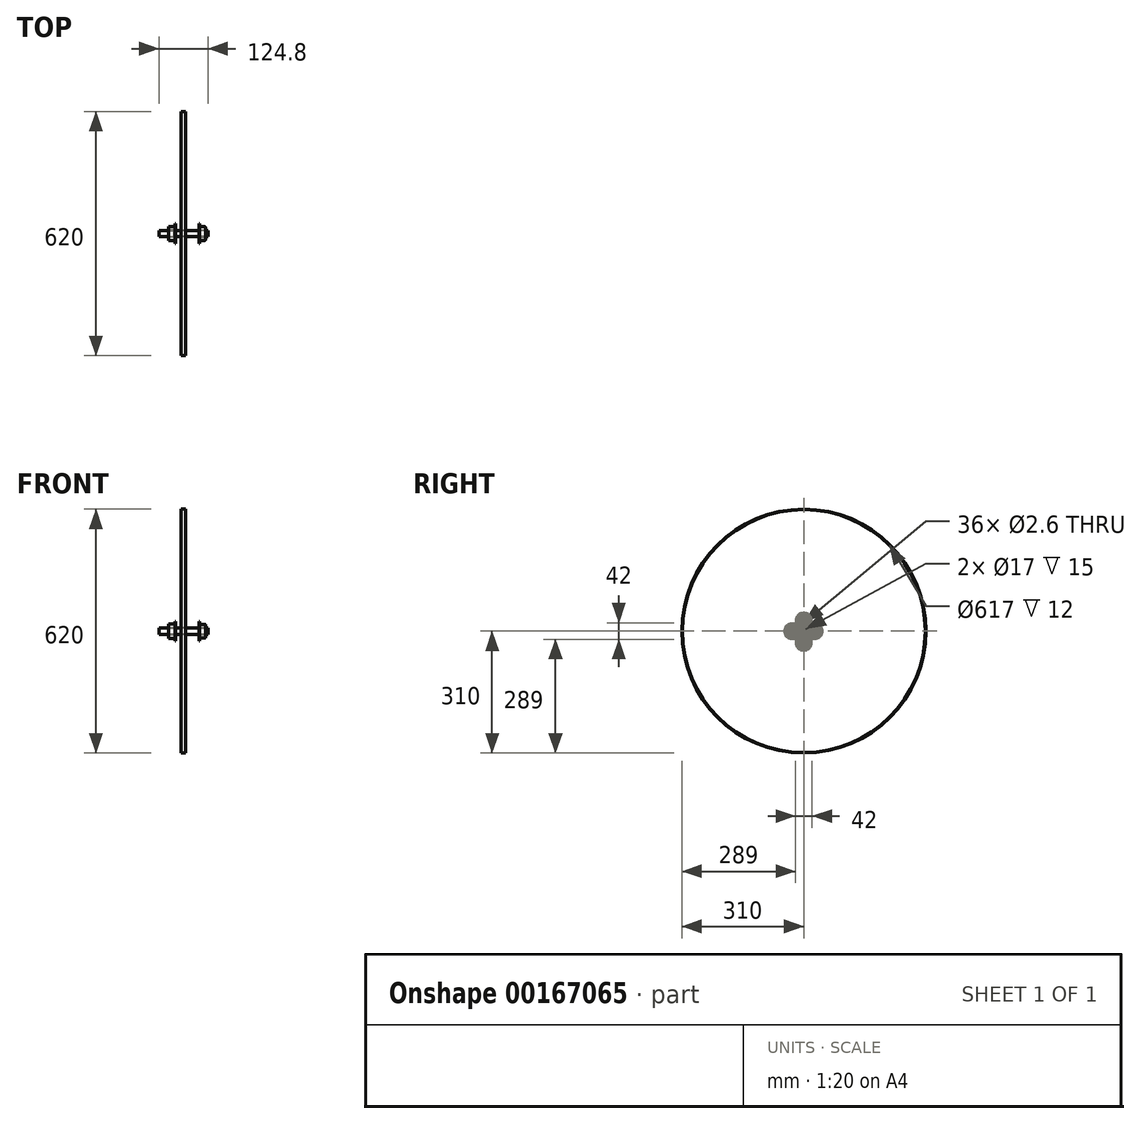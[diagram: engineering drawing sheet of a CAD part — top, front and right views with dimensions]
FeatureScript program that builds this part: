
annotation { "Feature Type Name" : "Feature", "Feature Type Description" : "" }
export const myFeature = defineFeature(function(context is Context, id is Id, definition is map)
    precondition{}
    {
        {
            var Q0;
            Q0=qCreatedBy(makeId("Top.planeOp"),FACE);
            var sketch = newSketch(context, id + "F0", { "sketchPlane" : qUnion([Q0])});
            skLineSegment(sketch, "E0", {"start": v(0, 0) * mm, "end": v(0, 18.2) * mm});
            skLineSegment(sketch, "E1", {"start": v(0, 18.2) * mm, "end": v(16.7, 18.2) * mm});
            skLineSegment(sketch, "E2", {"start": v(16.7, 18.2) * mm, "end": v(16.7, 25) * mm});
            skLineSegment(sketch, "E3", {"start": v(16.7, 25) * mm, "end": v(19, 25) * mm});
            skLineSegment(sketch, "E4", {"start": v(19, 25) * mm, "end": v(19, 8) * mm});
            skLineSegment(sketch, "E5", {"start": v(19, 8) * mm, "end": v(77.5, 8) * mm});
            skLineSegment(sketch, "E6", {"start": v(77.5, 8) * mm, "end": v(77.5, 25) * mm});
            skLineSegment(sketch, "E7", {"start": v(77.5, 25) * mm, "end": v(79.8, 25) * mm});
            skLineSegment(sketch, "E8", {"start": v(79.8, 25) * mm, "end": v(79.8, 17.6) * mm});
            skLineSegment(sketch, "E9", {"start": v(79.8, 17.6) * mm, "end": v(94.5, 17.6) * mm});
            skLineSegment(sketch, "E10", {"start": v(94.5, 17.6) * mm, "end": v(94.5, 0) * mm});
            skLineSegment(sketch, "E11", {"start": v(0, 0) * mm, "end": v(94.5, 0) * mm, "construction": true});
            skLineSegment(sketch, "E12", {"start": v(0, 0) * mm, "end": v(94.5, 0) * mm});
            skSolve(sketch);
        }
        {
            var Q0;
            Q0=makeQuery(id+"F0.imprint","IMPRINT",FACE,{"disambiguationData":[TD([[makeQuery(id+"F0.imprint","IMPRINT",EDGE,{"derivedFrom":sQuery(id+"F0.wireOp",EDGE,"E0")}),-1.0]])]});
            var Q1;
            Q1=sQuery(id+"F0.wireOp",EDGE,"E12");
            revolve(context, id + "F1", {"entities" : qUnion([Q0]), "axis" : qUnion([Q1]), "revolveType" : RevolveType.FULL});
        }
        {
            var Q0;
            Q0=makeQuery(id+"F1.opRevolve","SWEPT_FACE",FACE,{"disambiguationData":[OSD([sQuery(id+"F0.wireOp",EDGE,"E8")])]});
            var sketch = newSketch(context, id + "F2", { "sketchPlane" : qUnion([Q0])});
            skCircle(sketch, "E13", {"center": v(0, 21) * mm, "radius": 1.3 * mm});
            skCircle(sketch, "E14.1.0", {"center": v(-7.18, 19.73) * mm, "radius": 1.3 * mm});
            skCircle(sketch, "E14.2.0", {"center": v(-13.5, 16.09) * mm, "radius": 1.3 * mm});
            skCircle(sketch, "E14.3.0", {"center": v(-18.19, 10.5) * mm, "radius": 1.3 * mm});
            skCircle(sketch, "E14.4.0", {"center": v(-20.68, 3.65) * mm, "radius": 1.3 * mm});
            skCircle(sketch, "E14.5.0", {"center": v(-20.68, -3.65) * mm, "radius": 1.3 * mm});
            skCircle(sketch, "E14.6.0", {"center": v(-18.19, -10.5) * mm, "radius": 1.3 * mm});
            skCircle(sketch, "E14.7.0", {"center": v(-13.5, -16.09) * mm, "radius": 1.3 * mm});
            skCircle(sketch, "E14.8.0", {"center": v(-7.18, -19.73) * mm, "radius": 1.3 * mm});
            skCircle(sketch, "E14.9.0", {"center": v(0, -21) * mm, "radius": 1.3 * mm});
            skCircle(sketch, "E14.10.0", {"center": v(7.18, -19.73) * mm, "radius": 1.3 * mm});
            skCircle(sketch, "E14.11.0", {"center": v(13.5, -16.09) * mm, "radius": 1.3 * mm});
            skCircle(sketch, "E14.12.0", {"center": v(18.19, -10.5) * mm, "radius": 1.3 * mm});
            skCircle(sketch, "E14.13.0", {"center": v(20.68, -3.65) * mm, "radius": 1.3 * mm});
            skCircle(sketch, "E14.14.0", {"center": v(20.68, 3.65) * mm, "radius": 1.3 * mm});
            skCircle(sketch, "E14.15.0", {"center": v(18.19, 10.5) * mm, "radius": 1.3 * mm});
            skCircle(sketch, "E14.16.0", {"center": v(13.5, 16.09) * mm, "radius": 1.3 * mm});
            skCircle(sketch, "E14.17.0", {"center": v(7.18, 19.73) * mm, "radius": 1.3 * mm});
            skPoint(sketch, "E14.center", {"position": v(0, 0) * mm});
            skSolve(sketch);
        }
        {
            var Q0;
            Q0 = qSketchRegion(id + "F2", true);
            extrude(context, id + "F3", {"entities" : qUnion([Q0]), "operationType" : NewBodyOperationType.REMOVE, "endBound" : BoundingType.UP_TO_NEXT, "oppositeDirection" : true, "depth" : 25 * mm});
        }
        {
            var Q0;
            Q0=makeQuery(id+"F1.opRevolve","SWEPT_FACE",FACE,{"disambiguationData":[OSD([sQuery(id+"F0.wireOp",EDGE,"E2")])]});
            var sketch = newSketch(context, id + "F4", { "sketchPlane" : qUnion([Q0])});
            skCircle(sketch, "E15", {"center": v(0, 0) * mm, "radius": 21 * mm, "construction": true});
            skCircle(sketch, "E16", {"center": v(3.65, 20.68) * mm, "radius": 1.3 * mm});
            skLineSegment(sketch, "E17", {"start": v(3.65, 20.68) * mm, "end": v(0, 0) * mm, "construction": true});
            skCircle(sketch, "E18.1.0", {"center": v(-3.65, 20.68) * mm, "radius": 1.3 * mm});
            skCircle(sketch, "E18.2.0", {"center": v(-10.5, 18.19) * mm, "radius": 1.3 * mm});
            skCircle(sketch, "E18.3.0", {"center": v(-16.09, 13.5) * mm, "radius": 1.3 * mm});
            skCircle(sketch, "E18.4.0", {"center": v(-19.73, 7.18) * mm, "radius": 1.3 * mm});
            skCircle(sketch, "E18.5.0", {"center": v(-21, 0) * mm, "radius": 1.3 * mm});
            skCircle(sketch, "E18.6.0", {"center": v(-19.73, -7.18) * mm, "radius": 1.3 * mm});
            skCircle(sketch, "E18.7.0", {"center": v(-16.09, -13.5) * mm, "radius": 1.3 * mm});
            skCircle(sketch, "E18.8.0", {"center": v(-10.5, -18.19) * mm, "radius": 1.3 * mm});
            skCircle(sketch, "E18.9.0", {"center": v(-3.65, -20.68) * mm, "radius": 1.3 * mm});
            skCircle(sketch, "E18.10.0", {"center": v(3.65, -20.68) * mm, "radius": 1.3 * mm});
            skCircle(sketch, "E18.11.0", {"center": v(10.5, -18.19) * mm, "radius": 1.3 * mm});
            skCircle(sketch, "E18.12.0", {"center": v(16.09, -13.5) * mm, "radius": 1.3 * mm});
            skCircle(sketch, "E18.13.0", {"center": v(19.73, -7.18) * mm, "radius": 1.3 * mm});
            skCircle(sketch, "E18.14.0", {"center": v(21, 0) * mm, "radius": 1.3 * mm});
            skCircle(sketch, "E18.15.0", {"center": v(19.73, 7.18) * mm, "radius": 1.3 * mm});
            skCircle(sketch, "E18.16.0", {"center": v(16.09, 13.5) * mm, "radius": 1.3 * mm});
            skCircle(sketch, "E18.17.0", {"center": v(10.5, 18.19) * mm, "radius": 1.3 * mm});
            skSolve(sketch);
        }
        {
            var Q0;
            Q0 = qSketchRegion(id + "F4", true);
            extrude(context, id + "F5", {"entities" : qUnion([Q0]), "operationType" : NewBodyOperationType.REMOVE, "endBound" : BoundingType.UP_TO_NEXT, "oppositeDirection" : true, "depth" : 25 * mm});
        }
        {
            var Q0;
            Q0=makeQuery(id+"F1.opRevolve","SWEPT_EDGE",EDGE,{"disambiguationData":[OSD([sQuery(id+"F0.wireOp",EDGE,"E9"),sQuery(id+"F0.wireOp",EDGE,"E10")])]});
            fillet(context, id + "F6", {"entities" : qUnion([Q0]), "radius" : 2.5 * mm, "tangentPropagation" : true, "allowEdgeOverflow" : false});
        }
        {
            var Q0;
            Q0=makeQuery(id+"F1.opRevolve","SWEPT_FACE",FACE,{"disambiguationData":[OSD([sQuery(id+"F0.wireOp",EDGE,"E10")])]});
            var sketch = newSketch(context, id + "F7", { "sketchPlane" : qUnion([Q0])});
            skCircle(sketch, "E19", {"center": v(0, 0) * mm, "radius": 8.5 * mm});
            skSolve(sketch);
        }
        {
            var Q0;
            Q0=makeQuery(id+"F7.imprint","IMPRINT",FACE,{"disambiguationData":[TD([[makeQuery(id+"F7.imprint","IMPRINT",EDGE,{"derivedFrom":sQuery(id+"F7.wireOp",EDGE,"E19")}),1.0]])]});
            extrude(context, id + "F8", {"entities" : qUnion([Q0]), "operationType" : NewBodyOperationType.REMOVE, "oppositeDirection" : true, "depth" : 15 * mm});
        }
        {
            var Q0;
            Q0=makeQuery(id+"F1.opRevolve","SWEPT_FACE",FACE,{"disambiguationData":[OSD([sQuery(id+"F0.wireOp",EDGE,"E0")])]});
            var sketch = newSketch(context, id + "F9", { "sketchPlane" : qUnion([Q0])});
            skCircle(sketch, "E20", {"center": v(0, 0) * mm, "radius": 8.5 * mm});
            skSolve(sketch);
        }
        {
            var Q0;
            Q0=makeQuery(id+"F9.imprint","IMPRINT",FACE,{"disambiguationData":[TD([[makeQuery(id+"F9.imprint","IMPRINT",EDGE,{"derivedFrom":sQuery(id+"F9.wireOp",EDGE,"E20")}),1.0]])]});
            extrude(context, id + "F10", {"entities" : qUnion([Q0]), "operationType" : NewBodyOperationType.REMOVE, "oppositeDirection" : true, "depth" : 15 * mm});
        }
        {
            var Q0;
            Q0=makeQuery(id+"F1.opRevolve","SWEPT_FACE",FACE,{"disambiguationData":[OSD([sQuery(id+"F0.wireOp",EDGE,"E4")])]});
            var sketch = newSketch(context, id + "F11", { "sketchPlane" : qUnion([Q0])});
            skCircle(sketch, "E21", {"center": v(0, 0) * mm, "radius": 8 * mm});
            skSolve(sketch);
        }
        {
            var Q0;
            Q0 = qSketchRegion(id + "F11", true);
            extrude(context, id + "F12", {"entities" : qUnion([Q0]), "operationType" : NewBodyOperationType.ADD, "oppositeDirection" : true, "depth" : 43 * mm});
        }
        {
            var Q0;
            Q0=makeQuery(id+"F1.opRevolve","SWEPT_FACE",FACE,{"disambiguationData":[OSD([sQuery(id+"F0.wireOp",EDGE,"E6")])]});
            var sketch = newSketch(context, id + "F13", { "sketchPlane" : qUnion([Q0])});
            skCircle(sketch, "E22", {"center": v(0, 0) * mm, "radius": 8 * mm});
            skSolve(sketch);
        }
        {
            var Q0;
            Q0 = qSketchRegion(id + "F13", true);
            extrude(context, id + "F14", {"entities" : qUnion([Q0]), "operationType" : NewBodyOperationType.ADD, "oppositeDirection" : true, "depth" : 23.3 * mm});
        }
        {
            var Q0;
            Q0=makeQuery(id+"F12.opExtrude","CAP_FACE",FACE,{"disambiguationData":[OSD([sQuery(id+"F11.wireOp",EDGE,"E21")])],"isStart":false});
            cPlane(context, id + "F15", {"entities" : qUnion([Q0]), "cplaneType" : CPlaneType.OFFSET, "offset" : (124.8 / 2) * mm, "oppositeDirection" : true, "width" : 150 * mm, "height" : 150 * mm});
        }
        {
            var Q0;
            Q0=qCreatedBy(id+"F15.planeOp",FACE);
            var sketch = newSketch(context, id + "F16", { "sketchPlane" : qUnion([Q0])});
            skCircle(sketch, "E23", {"center": v(0, 0) * mm, "radius": 308.5 * mm});
            skCircle(sketch, "E24", {"center": v(0, 0) * mm, "radius": 310 * mm});
            skSolve(sketch);
        }
        {
            var Q0;
            Q0=makeQuery(id+"F16.imprint","IMPRINT",FACE,{"disambiguationData":[TD([[makeQuery(id+"F16.imprint","IMPRINT",EDGE,{"derivedFrom":sQuery(id+"F16.wireOp",EDGE,"E23")}),-1.0]])]});
            var Q1;
            Q1=sQuery(id+"F16.wireOp",EDGE,"E23");
            extrude(context, id + "F17", {"entities" : qUnion([Q0]), "surfaceEntities" : qUnion([Q1]), "endBound" : BoundingType.SYMMETRIC, "depth" : 12 * mm});
        }
    });
